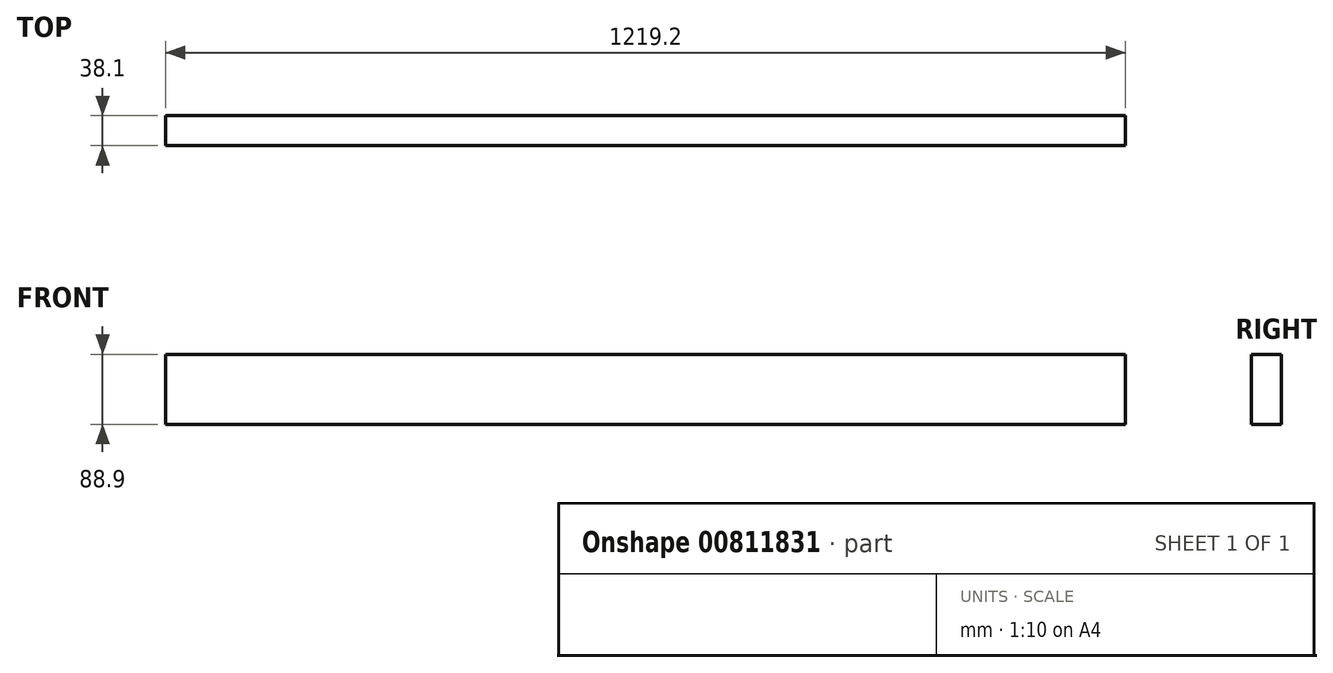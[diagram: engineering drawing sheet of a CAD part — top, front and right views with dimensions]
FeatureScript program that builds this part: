
annotation { "Feature Type Name" : "Feature", "Feature Type Description" : "" }
export const myFeature = defineFeature(function(context is Context, id is Id, definition is map)
    precondition{}
    {
        {
            var Q0;
            Q0=qCreatedBy(makeId("Front.planeOp"),FACE);
            var sketch = newSketch(context, id + "F0", { "sketchPlane" : qUnion([Q0])});
            skLineSegment(sketch, "E0.bottom", {"start": v(-608.88, 51.4) * mm, "end": v(610.32, 51.4) * mm});
            skLineSegment(sketch, "E0.top", {"start": v(-608.88, -37.5) * mm, "end": v(610.32, -37.5) * mm});
            skLineSegment(sketch, "E0.left", {"start": v(-608.88, 51.4) * mm, "end": v(-608.88, -37.5) * mm});
            skLineSegment(sketch, "E0.right", {"start": v(610.32, 51.4) * mm, "end": v(610.32, -37.5) * mm});
            skSolve(sketch);
        }
        {
            var Q0;
            Q0 = qSketchRegion(id + "F0", true);
            extrude(context, id + "F1", {"entities" : qUnion([Q0]), "endBound" : BoundingType.SYMMETRIC, "depth" : 38.1 * mm, "offsetDistance" : 25.4 * mm});
        }
    });
